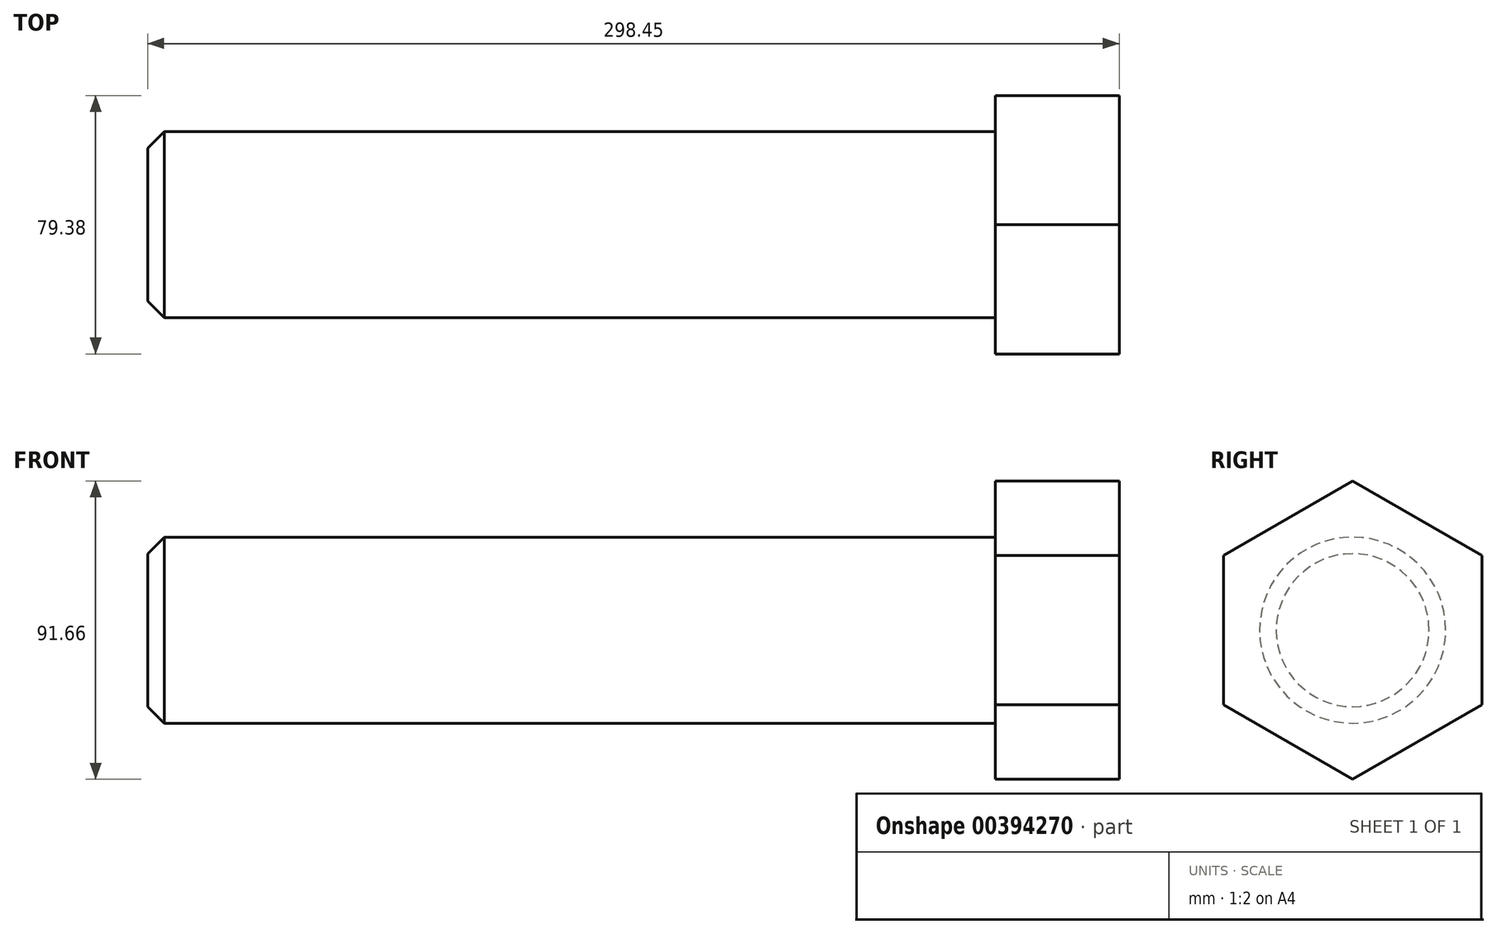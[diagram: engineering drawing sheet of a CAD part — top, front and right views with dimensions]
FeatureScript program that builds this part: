
annotation { "Feature Type Name" : "Feature", "Feature Type Description" : "" }
export const myFeature = defineFeature(function(context is Context, id is Id, definition is map)
    precondition{}
    {
        {
            var Q0;
            Q0=qCreatedBy(makeId("Front.planeOp"),FACE);
            var sketch = newSketch(context, id + "F0", { "sketchPlane" : qUnion([Q0])});
            skLineSegment(sketch, "E0", {"start": v(0, 0) * mm, "end": v(-260.35, 0) * mm});
            skLineSegment(sketch, "E1", {"start": v(-260.35, 28.57) * mm, "end": v(0, 28.57) * mm});
            skLineSegment(sketch, "E2", {"start": v(-260.35, 0) * mm, "end": v(-260.35, 28.57) * mm});
            skLineSegment(sketch, "E3", {"start": v(0, 0) * mm, "end": v(0, 28.57) * mm});
            skSolve(sketch);
        }
        {
            var Q0;
            Q0=makeQuery(id+"F0.imprint","IMPRINT",FACE,{"disambiguationData":[TD([[makeQuery(id+"F0.imprint","IMPRINT",EDGE,{"derivedFrom":sQuery(id+"F0.wireOp",EDGE,"E0")}),-1.0]])]});
            var Q1;
            Q1=sQuery(id+"F0.wireOp",EDGE,"E0");
            revolve(context, id + "F1", {"entities" : qUnion([Q0]), "axis" : qUnion([Q1]), "revolveType" : RevolveType.FULL});
        }
        {
            var Q0;
            Q0=qCreatedBy(makeId("Right.planeOp"),FACE);
            var sketch = newSketch(context, id + "F2", { "sketchPlane" : qUnion([Q0])});
            skCircle(sketch, "E4.cCircle", {"center": v(0, 0) * mm, "radius": 45.83 * mm, "construction": true});
            skLineSegment(sketch, "E4.0", {"start": v(0, -45.83) * mm, "end": v(-39.69, -22.91) * mm});
            skLineSegment(sketch, "E4.1", {"start": v(-39.69, -22.91) * mm, "end": v(-39.69, 22.91) * mm});
            skLineSegment(sketch, "E4.2", {"start": v(-39.69, 22.91) * mm, "end": v(0, 45.83) * mm});
            skLineSegment(sketch, "E4.3", {"start": v(0, 45.83) * mm, "end": v(39.69, 22.91) * mm});
            skLineSegment(sketch, "E4.4", {"start": v(39.69, 22.91) * mm, "end": v(39.69, -22.91) * mm});
            skLineSegment(sketch, "E4.5", {"start": v(39.69, -22.91) * mm, "end": v(0, -45.83) * mm});
            skSolve(sketch);
        }
        {
            var Q0;
            Q0=makeQuery(id+"F2.imprint","IMPRINT",FACE,{"disambiguationData":[TD([[makeQuery(id+"F2.imprint","IMPRINT",EDGE,{"derivedFrom":sQuery(id+"F2.wireOp",EDGE,"E4.0")}),-1.0]])]});
            var Q1;
            Q1=makeQuery(id+"F1.opRevolve","SWEPT_FACE",FACE,{"disambiguationData":[OSD([sQuery(id+"F0.wireOp",EDGE,"E3")])]});
            extrude(context, id + "F3", {"entities" : qUnion([Q0, Q1]), "operationType" : NewBodyOperationType.ADD, "depth" : 38.1 * mm});
        }
        {
            var Q0;
            Q0=makeQuery(id+"F1.opRevolve","SWEPT_EDGE",EDGE,{"disambiguationData":[OSD([sQuery(id+"F0.wireOp",EDGE,"E1"),sQuery(id+"F0.wireOp",EDGE,"E2")])]});
            chamfer(context, id + "F4", {"entities" : qUnion([Q0]), "width" : 5.08 * mm, "tangentPropagation" : true});
        }
    });
